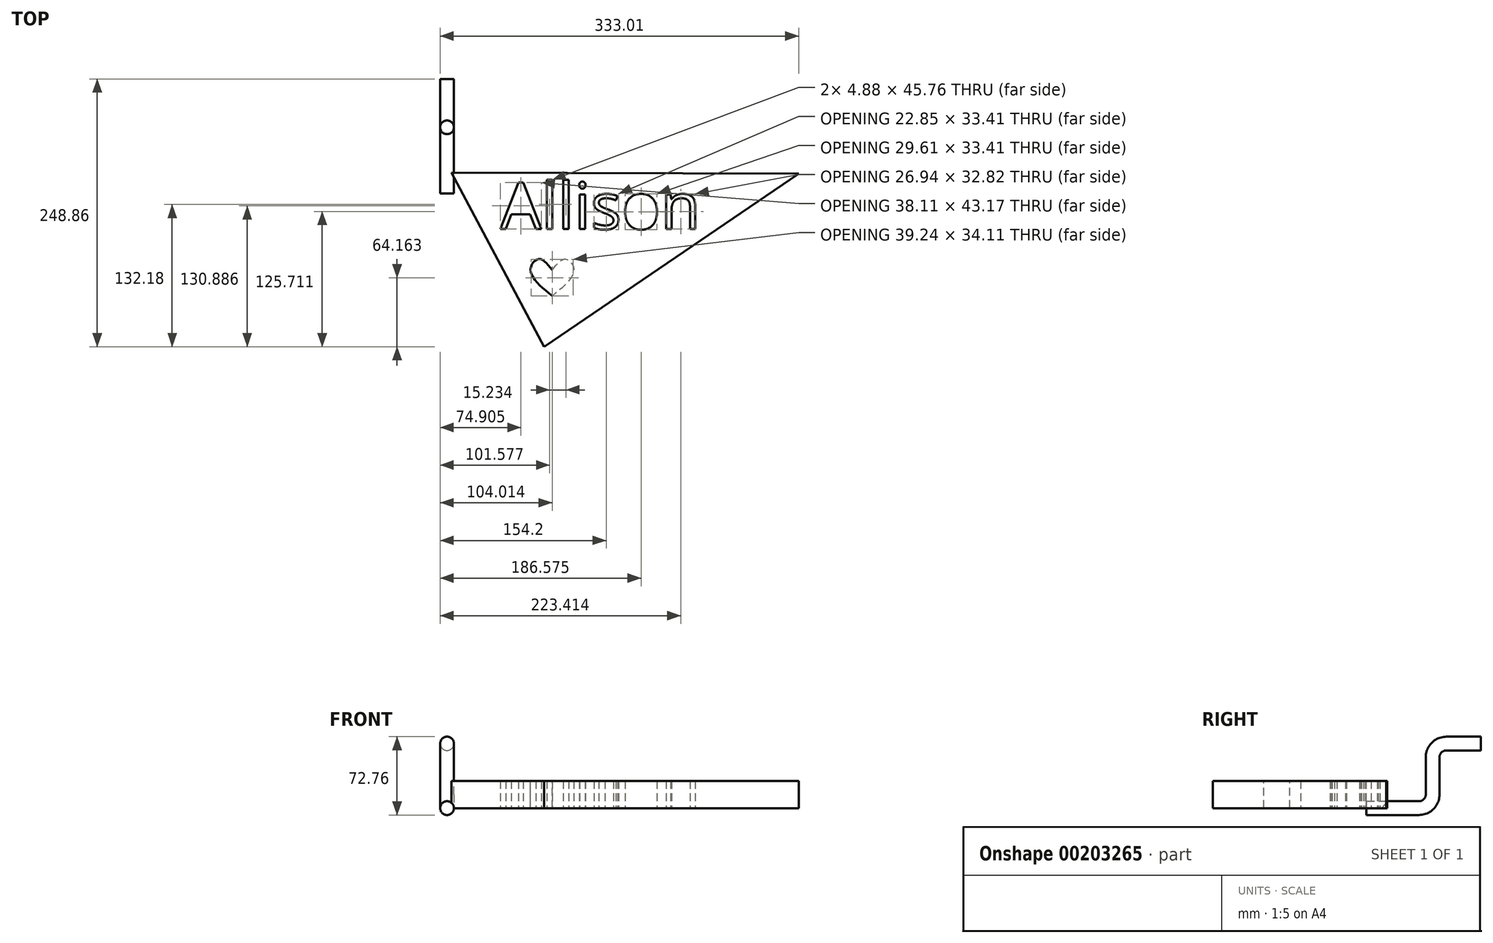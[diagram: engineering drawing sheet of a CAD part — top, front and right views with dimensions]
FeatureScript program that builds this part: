
annotation { "Feature Type Name" : "Feature", "Feature Type Description" : "" }
export const myFeature = defineFeature(function(context is Context, id is Id, definition is map)
    precondition{}
    {
        {
            var Q0;
            Q0=qCreatedBy(makeId("Right.planeOp"),FACE);
            var sketch = newSketch(context, id + "F0", { "sketchPlane" : qUnion([Q0])});
            skLineSegment(sketch, "E0", {"start": v(0, 0) * mm, "end": v(48.87, 0) * mm});
            skLineSegment(sketch, "E1", {"start": v(61.57, 12.7) * mm, "end": v(61.57, 47.3) * mm});
            skLineSegment(sketch, "E2", {"start": v(74.27, 60) * mm, "end": v(106.46, 60) * mm});
            skPoint(sketch, "E3.visualSharp", {"position": v(61.57, 60) * mm});
            skArc(sketch, "E3.filletArc", {"start": v(74.27, 60) * mm, "mid": v(65.29, 56.28) * mm, "end": v(61.57, 47.3) * mm});
            skPoint(sketch, "E4.visualSharp", {"position": v(61.57, 0) * mm});
            skArc(sketch, "E4.filletArc", {"start": v(48.87, 0) * mm, "mid": v(57.85, 3.72) * mm, "end": v(61.57, 12.7) * mm});
            skSolve(sketch);
        }
        {
            var Q0;
            Q0=qCreatedBy(makeId("Front.planeOp"),FACE);
            var sketch = newSketch(context, id + "F1", { "sketchPlane" : qUnion([Q0])});
            skCircle(sketch, "E5", {"center": v(0, 0) * mm, "radius": 6.38 * mm});
            skSolve(sketch);
        }
        {
            var Q0;
            Q0=makeQuery(id+"F1.imprint","IMPRINT",FACE,{"disambiguationData":[TD([[makeQuery(id+"F1.imprint","IMPRINT",EDGE,{"derivedFrom":sQuery(id+"F1.wireOp",EDGE,"E5")}),1.0]])]});
            var Q1;
            Q1=sQuery(id+"F0.wireOp",EDGE,"E0");
            var Q2;
            Q2=sQuery(id+"F0.wireOp",EDGE,"E4.filletArc");
            var Q3;
            Q3=sQuery(id+"F0.wireOp",EDGE,"E1");
            var Q4;
            Q4=sQuery(id+"F0.wireOp",EDGE,"E3.filletArc");
            var Q5;
            Q5=sQuery(id+"F0.wireOp",EDGE,"E2");
            sweep(context, id + "F2", {"profiles" : qUnion([Q0]), "path" : qUnion([Q1, Q2, Q3, Q4, Q5])});
        }
        {
            var Q0;
            Q0=qCreatedBy(makeId("Top.planeOp"),FACE);
            var sketch = newSketch(context, id + "F3", { "sketchPlane" : qUnion([Q0])});
            skLineSegment(sketch, "E6", {"start": v(4.19, 19.52) * mm, "end": v(326.63, 18.48) * mm});
            skLineSegment(sketch, "E7", {"start": v(326.63, 18.48) * mm, "end": v(90.28, -142.4) * mm});
            skLineSegment(sketch, "E8", {"start": v(90.28, -142.4) * mm, "end": v(4.19, 19.52) * mm});
            skText(sketch, "E9", { "text": "Allison", "fontName": "OpenSans-Regular.ttf"});
            const initialGuessF3  = {"E9": [0.04947, -0.0331, 1, 0, 0.04336]};
            skSetInitialGuess(sketch, initialGuessF3);
            skSolve(sketch);
        }
        {
            var Q0;
            Q0 = qSketchRegion(id + "F3", true);
            extrude(context, id + "F4", {"entities" : qUnion([Q0]), "operationType" : NewBodyOperationType.ADD, "depth" : 25.4 * mm});
        }
        {
            var Q0;
            Q0=makeQuery(id+"F4.opExtrude","CAP_FACE",FACE,{"disambiguationData":[OSD([sQuery(id+"F3.wireOp",EDGE,"E6"),sQuery(id+"F3.wireOp",EDGE,"E7"),sQuery(id+"F3.wireOp",EDGE,"E8"),sQuery(id+"F3.wireOp",EDGE,"E9.sketch_text.stroke-0"),sQuery(id+"F3.wireOp",EDGE,"E9.sketch_text.stroke-1"),sQuery(id+"F3.wireOp",EDGE,"E9.sketch_text.stroke-2"),sQuery(id+"F3.wireOp",EDGE,"E9.sketch_text.stroke-3"),sQuery(id+"F3.wireOp",EDGE,"E9.sketch_text.stroke-4"),sQuery(id+"F3.wireOp",EDGE,"E9.sketch_text.stroke-5"),sQuery(id+"F3.wireOp",EDGE,"E9.sketch_text.stroke-6"),sQuery(id+"F3.wireOp",EDGE,"E9.sketch_text.stroke-7"),sQuery(id+"F3.wireOp",EDGE,"E9.sketch_text.stroke-13"),sQuery(id+"F3.wireOp",EDGE,"E9.sketch_text.stroke-14"),sQuery(id+"F3.wireOp",EDGE,"E9.sketch_text.stroke-15"),sQuery(id+"F3.wireOp",EDGE,"E9.sketch_text.stroke-16"),sQuery(id+"F3.wireOp",EDGE,"E9.sketch_text.stroke-17"),sQuery(id+"F3.wireOp",EDGE,"E9.sketch_text.stroke-18"),sQuery(id+"F3.wireOp",EDGE,"E9.sketch_text.stroke-19"),sQuery(id+"F3.wireOp",EDGE,"E9.sketch_text.stroke-20"),sQuery(id+"F3.wireOp",EDGE,"E9.sketch_text.stroke-21"),sQuery(id+"F3.wireOp",EDGE,"E9.sketch_text.stroke-22"),sQuery(id+"F3.wireOp",EDGE,"E9.sketch_text.stroke-23"),sQuery(id+"F3.wireOp",EDGE,"E9.sketch_text.stroke-24"),sQuery(id+"F3.wireOp",EDGE,"E9.sketch_text.stroke-25"),sQuery(id+"F3.wireOp",EDGE,"E9.sketch_text.stroke-26"),sQuery(id+"F3.wireOp",EDGE,"E9.sketch_text.stroke-27"),sQuery(id+"F3.wireOp",EDGE,"E9.sketch_text.stroke-28"),sQuery(id+"F3.wireOp",EDGE,"E9.sketch_text.stroke-29"),sQuery(id+"F3.wireOp",EDGE,"E9.sketch_text.stroke-30"),sQuery(id+"F3.wireOp",EDGE,"E9.sketch_text.stroke-31"),sQuery(id+"F3.wireOp",EDGE,"E9.sketch_text.stroke-32"),sQuery(id+"F3.wireOp",EDGE,"E9.sketch_text.stroke-33"),sQuery(id+"F3.wireOp",EDGE,"E9.sketch_text.stroke-34"),sQuery(id+"F3.wireOp",EDGE,"E9.sketch_text.stroke-35"),sQuery(id+"F3.wireOp",EDGE,"E9.sketch_text.stroke-36"),sQuery(id+"F3.wireOp",EDGE,"E9.sketch_text.stroke-37"),sQuery(id+"F3.wireOp",EDGE,"E9.sketch_text.stroke-38"),sQuery(id+"F3.wireOp",EDGE,"E9.sketch_text.stroke-39"),sQuery(id+"F3.wireOp",EDGE,"E9.sketch_text.stroke-40"),sQuery(id+"F3.wireOp",EDGE,"E9.sketch_text.stroke-41"),sQuery(id+"F3.wireOp",EDGE,"E9.sketch_text.stroke-42"),sQuery(id+"F3.wireOp",EDGE,"E9.sketch_text.stroke-43"),sQuery(id+"F3.wireOp",EDGE,"E9.sketch_text.stroke-44"),sQuery(id+"F3.wireOp",EDGE,"E9.sketch_text.stroke-45"),sQuery(id+"F3.wireOp",EDGE,"E9.sketch_text.stroke-46"),sQuery(id+"F3.wireOp",EDGE,"E9.sketch_text.stroke-47"),sQuery(id+"F3.wireOp",EDGE,"E9.sketch_text.stroke-48"),sQuery(id+"F3.wireOp",EDGE,"E9.sketch_text.stroke-49"),sQuery(id+"F3.wireOp",EDGE,"E9.sketch_text.stroke-50"),sQuery(id+"F3.wireOp",EDGE,"E9.sketch_text.stroke-51"),sQuery(id+"F3.wireOp",EDGE,"E9.sketch_text.stroke-52"),sQuery(id+"F3.wireOp",EDGE,"E9.sketch_text.stroke-53"),sQuery(id+"F3.wireOp",EDGE,"E9.sketch_text.stroke-54"),sQuery(id+"F3.wireOp",EDGE,"E9.sketch_text.stroke-55"),sQuery(id+"F3.wireOp",EDGE,"E9.sketch_text.stroke-56"),sQuery(id+"F3.wireOp",EDGE,"E9.sketch_text.stroke-57"),sQuery(id+"F3.wireOp",EDGE,"E9.sketch_text.stroke-58"),sQuery(id+"F3.wireOp",EDGE,"E9.sketch_text.stroke-59"),sQuery(id+"F3.wireOp",EDGE,"E9.sketch_text.stroke-60"),sQuery(id+"F3.wireOp",EDGE,"E9.sketch_text.stroke-61"),sQuery(id+"F3.wireOp",EDGE,"E9.sketch_text.stroke-62"),sQuery(id+"F3.wireOp",EDGE,"E9.sketch_text.stroke-63"),sQuery(id+"F3.wireOp",EDGE,"E9.sketch_text.stroke-64"),sQuery(id+"F3.wireOp",EDGE,"E9.sketch_text.stroke-65"),sQuery(id+"F3.wireOp",EDGE,"E9.sketch_text.stroke-66"),sQuery(id+"F3.wireOp",EDGE,"E9.sketch_text.stroke-75"),sQuery(id+"F3.wireOp",EDGE,"E9.sketch_text.stroke-76"),sQuery(id+"F3.wireOp",EDGE,"E9.sketch_text.stroke-77"),sQuery(id+"F3.wireOp",EDGE,"E9.sketch_text.stroke-78"),sQuery(id+"F3.wireOp",EDGE,"E9.sketch_text.stroke-79"),sQuery(id+"F3.wireOp",EDGE,"E9.sketch_text.stroke-80"),sQuery(id+"F3.wireOp",EDGE,"E9.sketch_text.stroke-81"),sQuery(id+"F3.wireOp",EDGE,"E9.sketch_text.stroke-82"),sQuery(id+"F3.wireOp",EDGE,"E9.sketch_text.stroke-83"),sQuery(id+"F3.wireOp",EDGE,"E9.sketch_text.stroke-84"),sQuery(id+"F3.wireOp",EDGE,"E9.sketch_text.stroke-85"),sQuery(id+"F3.wireOp",EDGE,"E9.sketch_text.stroke-86"),sQuery(id+"F3.wireOp",EDGE,"E9.sketch_text.stroke-87"),sQuery(id+"F3.wireOp",EDGE,"E9.sketch_text.stroke-88"),sQuery(id+"F3.wireOp",EDGE,"E9.sketch_text.stroke-89"),sQuery(id+"F3.wireOp",EDGE,"E9.sketch_text.stroke-90"),sQuery(id+"F3.wireOp",EDGE,"E9.sketch_text.stroke-91")])],"isStart":false});
            var sketch = newSketch(context, id + "F5", { "sketchPlane" : qUnion([Q0])});
            skPoint(sketch, "E10.0.internal.snap0", {"position": v(97.63, -10.22) * mm});
            skPoint(sketch, "E10.3.internal.snap0", {"position": v(97.63, -10.22) * mm});
            skFitSpline(sketch, "E10", {"points": [v(97.63, -70.99) * mm, v(85.14, -60.9) * mm, v(77.56, -70.99) * mm, v(97.63, -95.29) * mm], "startDerivative": vector(-40.64, 51.76) * mm, "endDerivative": vector(70.25, -57.99) * mm});
            skFitSpline(sketch, "E11.MirrorCS", {"points": [v(97.63, -70.99) * mm, v(110.13, -60.9) * mm, v(117.7, -70.99) * mm, v(97.63, -95.29) * mm], "startDerivative": vector(40.64, 51.76) * mm, "endDerivative": vector(-70.25, -57.99) * mm});
            skSolve(sketch);
        }
        {
            var Q0;
            Q0 = qSketchRegion(id + "F5", true);
            extrude(context, id + "F6", {"entities" : qUnion([Q0]), "operationType" : NewBodyOperationType.REMOVE, "oppositeDirection" : true, "depth" : 25.4 * mm});
        }
    });
